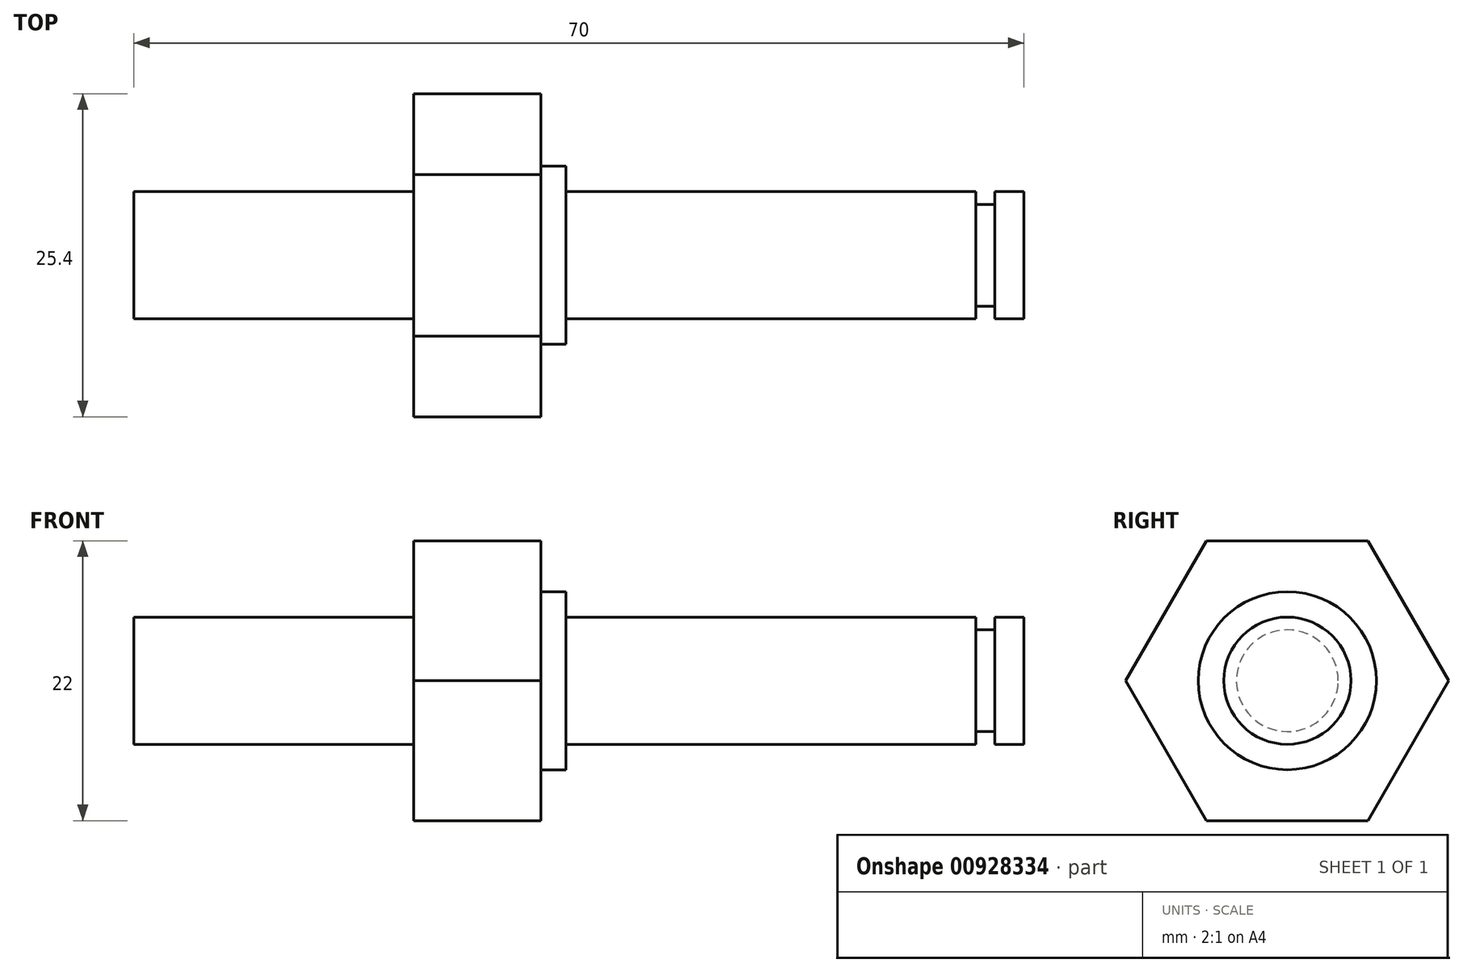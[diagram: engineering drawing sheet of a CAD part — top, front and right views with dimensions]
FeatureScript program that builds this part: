
annotation { "Feature Type Name" : "Feature", "Feature Type Description" : "" }
export const myFeature = defineFeature(function(context is Context, id is Id, definition is map)
    precondition{}
    {
        {
            var Q0;
            Q0=qCreatedBy(makeId("Right.planeOp"),FACE);
            var sketch = newSketch(context, id + "F0", { "sketchPlane" : qUnion([Q0])});
            skCircle(sketch, "E0.cCircle", {"center": v(0, 0) * mm, "radius": 12.7 * mm, "construction": true});
            skLineSegment(sketch, "E0.0", {"start": v(6.35, -11) * mm, "end": v(-6.35, -11) * mm});
            skLineSegment(sketch, "E0.1", {"start": v(-6.35, -11) * mm, "end": v(-12.7, 0) * mm});
            skLineSegment(sketch, "E0.2", {"start": v(-12.7, 0) * mm, "end": v(-6.35, 11) * mm});
            skLineSegment(sketch, "E0.3", {"start": v(-6.35, 11) * mm, "end": v(6.35, 11) * mm});
            skLineSegment(sketch, "E0.4", {"start": v(6.35, 11) * mm, "end": v(12.7, 0) * mm});
            skLineSegment(sketch, "E0.5", {"start": v(12.7, 0) * mm, "end": v(6.35, -11) * mm});
            skSolve(sketch);
        }
        {
            var Q0;
            Q0 = qSketchRegion(id + "F0", true);
            extrude(context, id + "F1", {"entities" : qUnion([Q0]), "oppositeDirection" : true, "depth" : 10 * mm, "offsetDistance" : 25 * mm});
        }
        {
            var Q0;
            Q0=makeQuery(id+"F1.opExtrude","CAP_FACE",FACE,{"disambiguationData":[OSD([sQuery(id+"F0.wireOp",EDGE,"E0.0"),sQuery(id+"F0.wireOp",EDGE,"E0.1"),sQuery(id+"F0.wireOp",EDGE,"E0.2"),sQuery(id+"F0.wireOp",EDGE,"E0.3"),sQuery(id+"F0.wireOp",EDGE,"E0.4"),sQuery(id+"F0.wireOp",EDGE,"E0.5")])],"isStart":true});
            var sketch = newSketch(context, id + "F2", { "sketchPlane" : qUnion([Q0])});
            skCircle(sketch, "E1", {"center": v(0, 0) * mm, "radius": 7 * mm});
            skSolve(sketch);
        }
        {
            var Q0;
            Q0 = qSketchRegion(id + "F2", true);
            extrude(context, id + "F3", {"entities" : qUnion([Q0]), "operationType" : NewBodyOperationType.ADD, "depth" : 2 * mm, "offsetDistance" : 25 * mm});
        }
        {
            var Q0;
            Q0=makeQuery(id+"F3.opExtrude","CAP_FACE",FACE,{"disambiguationData":[OSD([sQuery(id+"F2.wireOp",EDGE,"E1")])],"isStart":false});
            var sketch = newSketch(context, id + "F4", { "sketchPlane" : qUnion([Q0])});
            skCircle(sketch, "E2", {"center": v(0, 0) * mm, "radius": 5 * mm});
            skSolve(sketch);
        }
        {
            var Q0;
            Q0 = qSketchRegion(id + "F4", true);
            extrude(context, id + "F5", {"entities" : qUnion([Q0]), "operationType" : NewBodyOperationType.ADD, "depth" : 36 * mm, "offsetDistance" : 25 * mm});
        }
        {
            var Q0;
            Q0=qCreatedBy(makeId("Front.planeOp"),FACE);
            var sketch = newSketch(context, id + "F6", { "sketchPlane" : qUnion([Q0])});
            skLineSegment(sketch, "E3.bottom", {"start": v(34.2, -5.42) * mm, "end": v(35.7, -5.42) * mm});
            skLineSegment(sketch, "E3.top", {"start": v(34.2, -4) * mm, "end": v(35.7, -4) * mm});
            skLineSegment(sketch, "E3.left", {"start": v(34.2, -5.42) * mm, "end": v(34.2, -4) * mm});
            skLineSegment(sketch, "E3.right", {"start": v(35.7, -5.42) * mm, "end": v(35.7, -4) * mm});
            skSolve(sketch);
        }
        {
            var Q0;
            Q0 = qSketchRegion(id + "F6", true);
            var Q1;
            Q1=makeQuery(id+"F5.opExtrude","CAP_EDGE",EDGE,{"disambiguationData":[OSD([sQuery(id+"F4.wireOp",EDGE,"E2")])],"isStart":false});
            revolve(context, id + "F7", {"operationType" : NewBodyOperationType.REMOVE, "surfaceOperationType" : NewSurfaceOperationType.NEW, "entities" : qUnion([Q0]), "axis" : qUnion([Q1]), "revolveType" : RevolveType.FULL, "oppositeDirection" : true});
        }
        {
            var Q0;
            Q0=makeQuery(id+"F1.opExtrude","CAP_FACE",FACE,{"disambiguationData":[OSD([sQuery(id+"F0.wireOp",EDGE,"E0.0"),sQuery(id+"F0.wireOp",EDGE,"E0.1"),sQuery(id+"F0.wireOp",EDGE,"E0.2"),sQuery(id+"F0.wireOp",EDGE,"E0.3"),sQuery(id+"F0.wireOp",EDGE,"E0.4"),sQuery(id+"F0.wireOp",EDGE,"E0.5")])],"isStart":false});
            var sketch = newSketch(context, id + "F8", { "sketchPlane" : qUnion([Q0])});
            skCircle(sketch, "E4", {"center": v(0, 0) * mm, "radius": 5 * mm});
            skSolve(sketch);
        }
        {
            var Q0;
            Q0=makeQuery(id+"F8.imprint","IMPRINT",FACE,{"disambiguationData":[TD([[makeQuery(id+"F8.imprint","IMPRINT",EDGE,{"derivedFrom":sQuery(id+"F8.wireOp",EDGE,"E4")}),1.0]])]});
            var Q1;
            Q1=sQuery(id+"F8.wireOp",EDGE,"E4");
            extrude(context, id + "F9", {"entities" : qUnion([Q0]), "operationType" : NewBodyOperationType.ADD, "surfaceEntities" : qUnion([Q1]), "depth" : 22 * mm, "offsetDistance" : 25 * mm});
        }
    });
